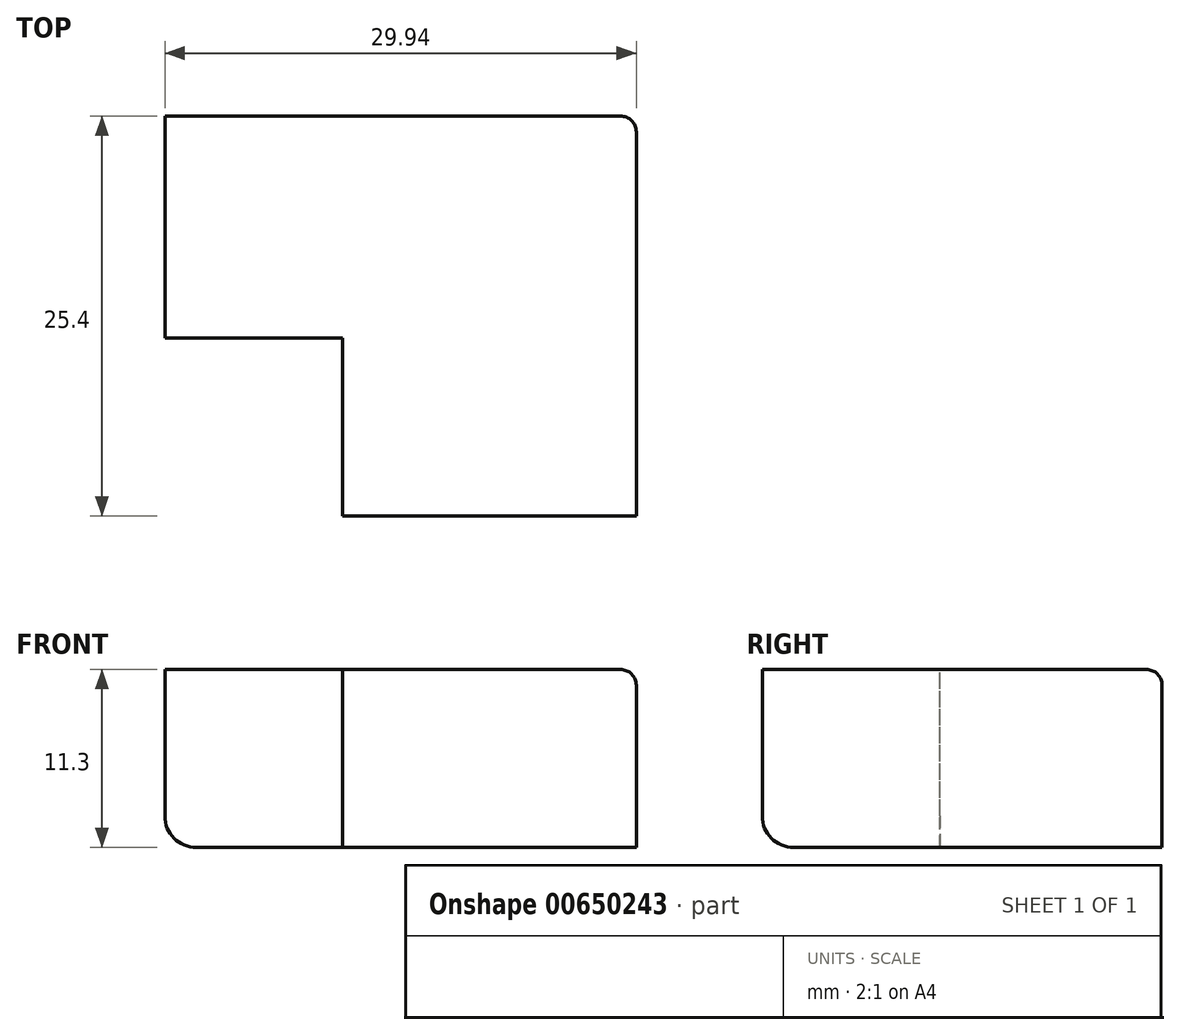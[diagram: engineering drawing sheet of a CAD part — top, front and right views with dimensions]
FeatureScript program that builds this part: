
annotation { "Feature Type Name" : "Feature", "Feature Type Description" : "" }
export const myFeature = defineFeature(function(context is Context, id is Id, definition is map)
    precondition{}
    {
        {
            var Q0;
            Q0=qCreatedBy(makeId("Top.planeOp"),FACE);
            var sketch = newSketch(context, id + "F0", { "sketchPlane" : qUnion([Q0])});
            skLineSegment(sketch, "E0.bottom", {"start": v(0, 0) * mm, "end": v(29.94, 0) * mm});
            skLineSegment(sketch, "E0.top", {"start": v(0, 25.4) * mm, "end": v(29.94, 25.4) * mm});
            skLineSegment(sketch, "E0.left", {"start": v(0, 0) * mm, "end": v(0, 25.4) * mm});
            skLineSegment(sketch, "E0.right", {"start": v(29.94, 0) * mm, "end": v(29.94, 25.4) * mm});
            skSolve(sketch);
        }
        {
            var Q0;
            Q0=makeQuery(id+"F0.imprint","IMPRINT",FACE,{"disambiguationData":[TD([[makeQuery(id+"F0.imprint","IMPRINT",EDGE,{"derivedFrom":sQuery(id+"F0.wireOp",EDGE,"E0.bottom")}),1.0]])]});
            extrude(context, id + "F1", {"entities" : qUnion([Q0]), "depth" : 11.3 * mm, "offsetDistance" : 25 * mm});
        }
        {
            var Q0;
            Q0=makeQuery(id+"F1.opExtrude","CAP_FACE",FACE,{"disambiguationData":[OSD([sQuery(id+"F0.wireOp",EDGE,"E0.bottom"),sQuery(id+"F0.wireOp",EDGE,"E0.top"),sQuery(id+"F0.wireOp",EDGE,"E0.left"),sQuery(id+"F0.wireOp",EDGE,"E0.right")])],"isStart":false});
            var sketch = newSketch(context, id + "F2", { "sketchPlane" : qUnion([Q0])});
            skLineSegment(sketch, "E1.bottom", {"start": v(0, 0) * mm, "end": v(11.3, 0) * mm});
            skLineSegment(sketch, "E1.top", {"start": v(0, 11.3) * mm, "end": v(11.3, 11.3) * mm});
            skLineSegment(sketch, "E1.left", {"start": v(0, 0) * mm, "end": v(0, 11.3) * mm});
            skLineSegment(sketch, "E1.right", {"start": v(11.3, 0) * mm, "end": v(11.3, 11.3) * mm});
            skSolve(sketch);
        }
        {
            var Q0;
            Q0=makeQuery(id+"F2.imprint","IMPRINT",FACE,{"disambiguationData":[TD([[makeQuery(id+"F2.imprint","IMPRINT",EDGE,{"derivedFrom":sQuery(id+"F2.wireOp",EDGE,"E1.bottom")}),1.0]])]});
            extrude(context, id + "F3", {"entities" : qUnion([Q0]), "operationType" : NewBodyOperationType.REMOVE, "oppositeDirection" : true, "depth" : 25 * mm, "offsetDistance" : 25 * mm});
        }
        {
            var Q0;
            Q0=makeQuery(id+"F1.opExtrude","CAP_EDGE",EDGE,{"disambiguationData":[OSD([sQuery(id+"F0.wireOp",EDGE,"E0.bottom")])],"isStart":true});
            var Q1;
            Q1=makeQuery(id+"F1.opExtrude","CAP_EDGE",EDGE,{"disambiguationData":[OSD([sQuery(id+"F0.wireOp",EDGE,"E0.left")])],"isStart":true});
            fillet(context, id + "F4", {"entities" : qUnion([Q0, Q1]), "radius" : 2 * mm, "tangentPropagation" : true, "allowEdgeOverflow" : false});
        }
        {
            var Q0;
            Q0=makeQuery(id+"F1.opExtrude","SWEPT_EDGE",EDGE,{"disambiguationData":[OSD([sQuery(id+"F0.wireOp",EDGE,"E0.top"),sQuery(id+"F0.wireOp",EDGE,"E0.right")])]});
            var Q1;
            Q1=makeQuery(id+"F1.opExtrude","CAP_EDGE",EDGE,{"disambiguationData":[OSD([sQuery(id+"F0.wireOp",EDGE,"E0.top")])],"isStart":false});
            var Q2;
            Q2=makeQuery(id+"F1.opExtrude","CAP_EDGE",EDGE,{"disambiguationData":[OSD([sQuery(id+"F0.wireOp",EDGE,"E0.right")])],"isStart":false});
            fillet(context, id + "F5", {"entities" : qUnion([Q0, Q1, Q2]), "radius" : 1 * mm, "tangentPropagation" : true, "allowEdgeOverflow" : false});
        }
    });
